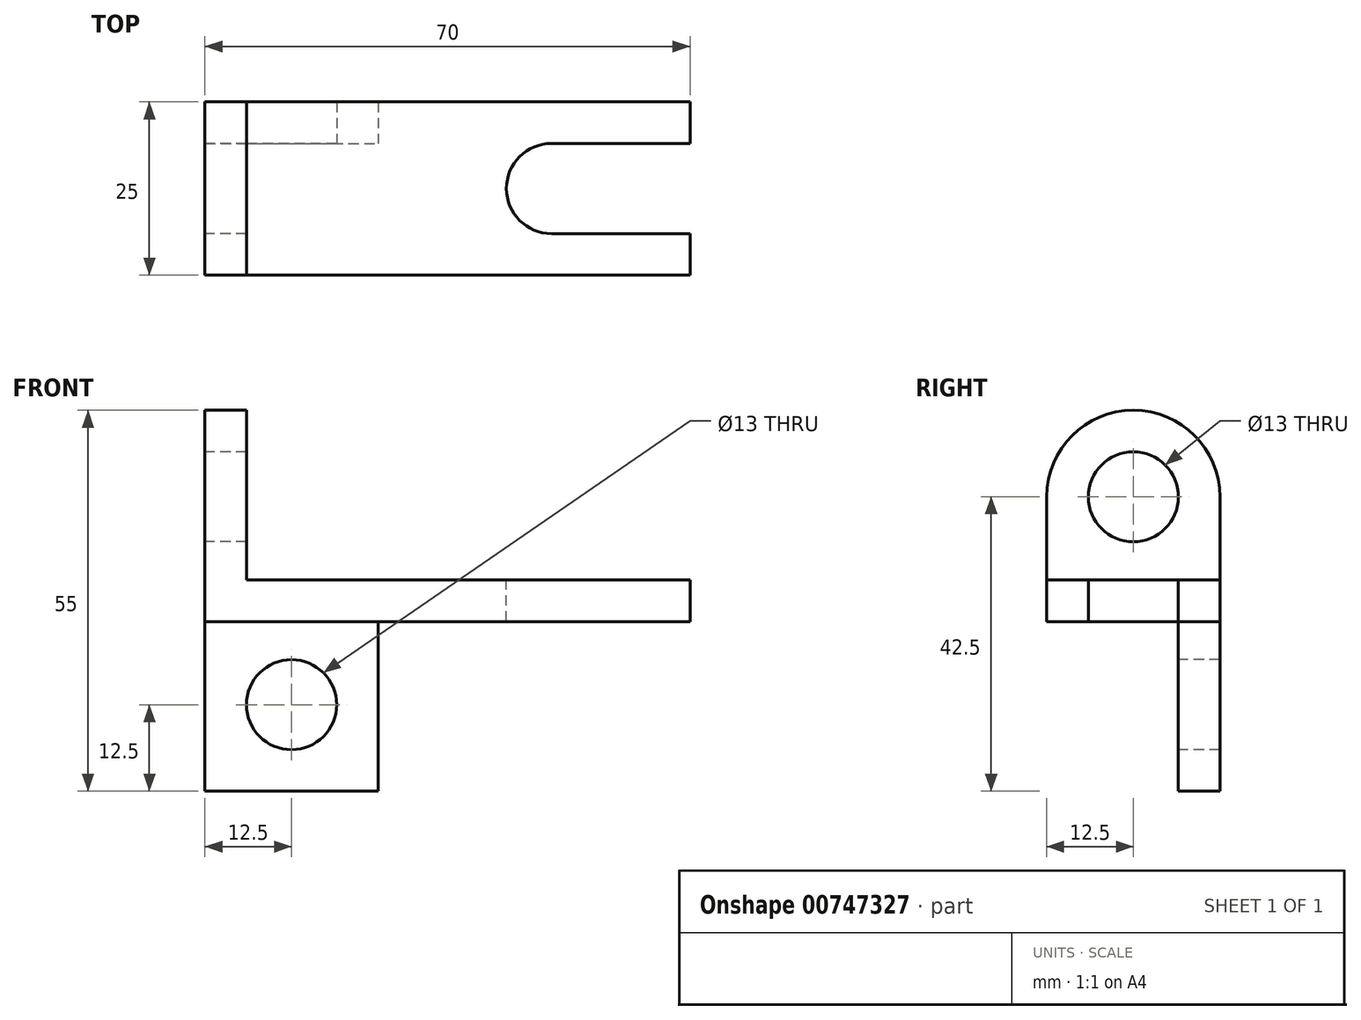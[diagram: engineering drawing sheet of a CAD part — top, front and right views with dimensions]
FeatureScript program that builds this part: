
annotation { "Feature Type Name" : "Feature", "Feature Type Description" : "" }
export const myFeature = defineFeature(function(context is Context, id is Id, definition is map)
    precondition{}
    {
        {
            var Q0;
            Q0=qCreatedBy(makeId("Front.planeOp"),FACE);
            var sketch = newSketch(context, id + "F0", { "sketchPlane" : qUnion([Q0])});
            skLineSegment(sketch, "E0", {"start": v(0, 0) * mm, "end": v(70, 0) * mm});
            skLineSegment(sketch, "E1", {"start": v(70, 0) * mm, "end": v(70, 6) * mm});
            skLineSegment(sketch, "E2", {"start": v(70, 6) * mm, "end": v(6, 6) * mm});
            skLineSegment(sketch, "E3", {"start": v(6, 6) * mm, "end": v(6, 30.5) * mm});
            skLineSegment(sketch, "E4", {"start": v(6, 30.5) * mm, "end": v(0, 30.5) * mm});
            skLineSegment(sketch, "E5", {"start": v(0, 30.5) * mm, "end": v(0, 0) * mm});
            skSolve(sketch);
        }
        {
            var Q0;
            Q0=makeQuery(id+"F0.imprint","IMPRINT",FACE,{"disambiguationData":[TD([[makeQuery(id+"F0.imprint","IMPRINT",EDGE,{"derivedFrom":sQuery(id+"F0.wireOp",EDGE,"E0")}),1.0]])]});
            extrude(context, id + "F1", {"entities" : qUnion([Q0]), "depth" : 25 * mm, "offsetDistance" : 25 * mm});
        }
        {
            var Q0;
            Q0=makeQuery(id+"F1.opExtrude","SWEPT_FACE",FACE,{"disambiguationData":[OSD([sQuery(id+"F0.wireOp",EDGE,"E2")])]});
            var sketch = newSketch(context, id + "F2", { "sketchPlane" : qUnion([Q0])});
            skLineSegment(sketch, "E6", {"start": v(70, -6) * mm, "end": v(50, -6) * mm});
            skLineSegment(sketch, "E7", {"start": v(50, -19) * mm, "end": v(70, -19) * mm});
            skLineSegment(sketch, "E8", {"start": v(70, -6) * mm, "end": v(70, -19) * mm});
            skArc(sketch, "E9", {"start": v(50, -6) * mm, "mid": v(43.5, -12.5) * mm, "end": v(50, -19) * mm});
            skSolve(sketch);
        }
        {
            var Q0;
            Q0=makeQuery(id+"F2.imprint","IMPRINT",FACE,{"disambiguationData":[TD([[makeQuery(id+"F2.imprint","IMPRINT",EDGE,{"derivedFrom":sQuery(id+"F2.wireOp",EDGE,"E6")}),1.0]])]});
            extrude(context, id + "F3", {"entities" : qUnion([Q0]), "operationType" : NewBodyOperationType.REMOVE, "oppositeDirection" : true, "depth" : 6 * mm, "offsetDistance" : 25 * mm});
        }
        {
            var Q0;
            Q0=makeQuery(id+"F1.opExtrude","SWEPT_FACE",FACE,{"disambiguationData":[OSD([sQuery(id+"F0.wireOp",EDGE,"E5")])]});
            var sketch = newSketch(context, id + "F4", { "sketchPlane" : qUnion([Q0])});
            skArc(sketch, "E10", {"start": v(25, 18) * mm, "mid": v(12.5, 30.5) * mm, "end": v(0, 18) * mm});
            skPoint(sketch, "E10.startSnap0", {"position": v(25, 15.25) * mm});
            skPoint(sketch, "E10.startSnap1", {"position": v(6.25, 18) * mm});
            skLineSegment(sketch, "E11", {"start": v(0, 18) * mm, "end": v(0, 30.5) * mm});
            skLineSegment(sketch, "E12", {"start": v(0, 30.5) * mm, "end": v(25, 30.5) * mm});
            skLineSegment(sketch, "E13", {"start": v(25, 30.5) * mm, "end": v(25, 18) * mm});
            skSolve(sketch);
        }
        {
            var Q0;
            {var subQ0=sQuery(id+"F4.wireOp",EDGE,"E13");Q0=makeQuery(id+"F4.imprint","IMPRINT",FACE,{"disambiguationData":[TD([[makeQuery(id+"F4.imprint","IMPRINT",EDGE,{"derivedFrom":subQ0}),-1.0]])]});}
            var Q1;
            {var subQ0=sQuery(id+"F4.wireOp",EDGE,"E11");Q1=makeQuery(id+"F4.imprint","IMPRINT",FACE,{"disambiguationData":[TD([[makeQuery(id+"F4.imprint","IMPRINT",EDGE,{"derivedFrom":subQ0}),1.0]])]});}
            extrude(context, id + "F5", {"entities" : qUnion([Q0, Q1]), "operationType" : NewBodyOperationType.REMOVE, "oppositeDirection" : true, "depth" : 6 * mm, "offsetDistance" : 25 * mm});
        }
        {
            var Q0;
            Q0=makeQuery(id+"F1.opExtrude","SWEPT_FACE",FACE,{"disambiguationData":[OSD([sQuery(id+"F0.wireOp",EDGE,"E5")])]});
            var sketch = newSketch(context, id + "F6", { "sketchPlane" : qUnion([Q0])});
            skCircle(sketch, "E14", {"center": v(12.5, 18) * mm, "radius": 6.5 * mm});
            skSolve(sketch);
        }
        {
            var Q0;
            Q0=makeQuery(id+"F6.imprint","IMPRINT",FACE,{"disambiguationData":[TD([[makeQuery(id+"F6.imprint","IMPRINT",EDGE,{"derivedFrom":sQuery(id+"F6.wireOp",EDGE,"E14")}),1.0]])]});
            extrude(context, id + "F7", {"entities" : qUnion([Q0]), "operationType" : NewBodyOperationType.REMOVE, "oppositeDirection" : true, "depth" : 6 * mm, "offsetDistance" : 25 * mm});
        }
        {
            var Q0;
            Q0=makeQuery(id+"F1.opExtrude","SWEPT_FACE",FACE,{"disambiguationData":[OSD([sQuery(id+"F0.wireOp",EDGE,"E0")])]});
            var sketch = newSketch(context, id + "F8", { "sketchPlane" : qUnion([Q0])});
            skLineSegment(sketch, "E15.bottom", {"start": v(0, 0) * mm, "end": v(25, 0) * mm});
            skLineSegment(sketch, "E15.top", {"start": v(0, 6) * mm, "end": v(25, 6) * mm});
            skLineSegment(sketch, "E15.left", {"start": v(0, 0) * mm, "end": v(0, 6) * mm});
            skLineSegment(sketch, "E15.right", {"start": v(25, 0) * mm, "end": v(25, 6) * mm});
            skSolve(sketch);
        }
        {
            var Q0;
            Q0=makeQuery(id+"F8.imprint","IMPRINT",FACE,{"disambiguationData":[TD([[makeQuery(id+"F8.imprint","IMPRINT",EDGE,{"derivedFrom":sQuery(id+"F8.wireOp",EDGE,"E15.bottom")}),1.0]])]});
            extrude(context, id + "F9", {"entities" : qUnion([Q0]), "operationType" : NewBodyOperationType.ADD, "depth" : 24.5 * mm, "offsetDistance" : 25 * mm});
        }
        {
            var Q0;
            Q0=makeQuery(id+"F9.opExtrude","SWEPT_FACE",FACE,{"disambiguationData":[OSD([sQuery(id+"F8.wireOp",EDGE,"E15.top")])]});
            var sketch = newSketch(context, id + "F10", { "sketchPlane" : qUnion([Q0])});
            skLineSegment(sketch, "E16", {"start": v(0, 0) * mm, "end": v(0, -24.5) * mm});
            skLineSegment(sketch, "E17", {"start": v(25, -24.5) * mm, "end": v(25, 0) * mm});
            skArc(sketch, "E18", {"start": v(0, -12) * mm, "mid": v(12.5, -24.5) * mm, "end": v(25, -12) * mm});
            skCircle(sketch, "E19", {"center": v(12.5, -12) * mm, "radius": 6.5 * mm});
            skLineSegment(sketch, "E20", {"start": v(0, -12) * mm, "end": v(0, -24.5) * mm});
            skLineSegment(sketch, "E21", {"start": v(25, -24.5) * mm, "end": v(25, -12) * mm});
            skLineSegment(sketch, "E22", {"start": v(25, -24.5) * mm, "end": v(0, -24.5) * mm});
            skSolve(sketch);
        }
        {
            var Q0;
            {var subQ0=sQuery(id+"F10.wireOp",EDGE,"E20");Q0=makeQuery(id+"F10.imprint","IMPRINT",FACE,{"disambiguationData":[TD([[makeQuery(id+"F10.imprint","IMPRINT",EDGE,{"derivedFrom":subQ0}),-1.0]])]});}
            var Q1;
            {var subQ0=sQuery(id+"F10.wireOp",EDGE,"E21");Q1=makeQuery(id+"F10.imprint","IMPRINT",FACE,{"disambiguationData":[TD([[makeQuery(id+"F10.imprint","IMPRINT",EDGE,{"derivedFrom":subQ0}),1.0]])]});}
            var Q2;
            Q2=makeQuery(id+"F10.imprint","IMPRINT",FACE,{"disambiguationData":[TD([[makeQuery(id+"F10.imprint","IMPRINT",EDGE,{"derivedFrom":sQuery(id+"F10.wireOp",EDGE,"E19")}),1.0]])]});
            extrude(context, id + "F11", {"entities" : qUnion([Q0, Q1, Q2]), "operationType" : NewBodyOperationType.REMOVE, "oppositeDirection" : true, "depth" : 6 * mm, "offsetDistance" : 25 * mm});
        }
    });
